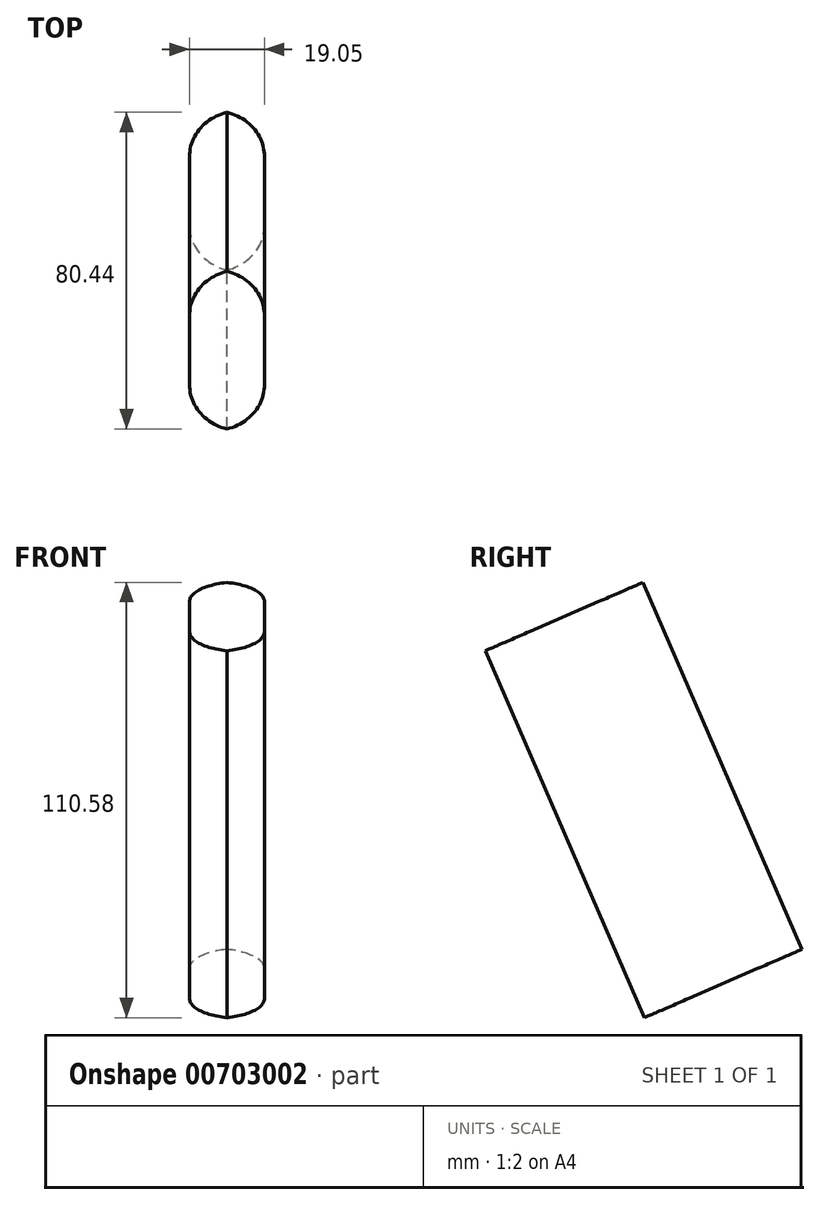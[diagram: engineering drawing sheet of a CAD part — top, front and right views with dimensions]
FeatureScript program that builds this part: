
annotation { "Feature Type Name" : "Feature", "Feature Type Description" : "" }
export const myFeature = defineFeature(function(context is Context, id is Id, definition is map)
    precondition{}
    {
        {
            var Q0;
            Q0=qCreatedBy(makeId("Right.planeOp"),FACE);
            var sketch = newSketch(context, id + "F0", { "sketchPlane" : qUnion([Q0])});
            skLineSegment(sketch, "E0", {"start": v(3.78, 1.74) * mm, "end": v(44.56, 19.41) * mm});
            skLineSegment(sketch, "E1", {"start": v(4.17, 112.64) * mm, "end": v(-36.62, 94.96) * mm});
            skLineSegment(sketch, "E2", {"start": v(44.56, 19.41) * mm, "end": v(4.17, 112.64) * mm});
            skLineSegment(sketch, "E3", {"start": v(3.78, 1.74) * mm, "end": v(-36.62, 94.96) * mm});
            skSolve(sketch);
        }
        {
            var Q0;
            Q0=makeQuery(id+"F0.imprint","IMPRINT",FACE,{"disambiguationData":[TD([[makeQuery(id+"F0.imprint","IMPRINT",EDGE,{"derivedFrom":sQuery(id+"F0.wireOp",EDGE,"E0")}),1.0]])]});
            extrude(context, id + "F1", {"entities" : qUnion([Q0]), "depth" : 19.05 * mm, "offsetDistance" : 25.4 * mm});
        }
        {
            var Q0;
            Q0=makeQuery(id+"F1.opExtrude","CAP_EDGE",EDGE,{"disambiguationData":[OSD([sQuery(id+"F0.wireOp",EDGE,"pg5uUo5L-hMJ6-0TQC-OhPI-5jsaEnWjynJh")])],"isStart":false});
            var Q1;
            Q1=makeQuery(id+"F1.opExtrude","CAP_EDGE",EDGE,{"disambiguationData":[OSD([sQuery(id+"F0.wireOp",EDGE,"pg5uUo5L-hMJ6-0TQC-OhPI-5jsaEnWjynJh")])],"isStart":true});
            var Q2;
            Q2=makeQuery(id+"F1.opExtrude","CAP_EDGE",EDGE,{"disambiguationData":[OSD([sQuery(id+"F0.wireOp",EDGE,"cwDIRSyl-O5Kx-4CkM-n87C-obHUcLD1ZQiq")])],"isStart":false});
            var Q3;
            Q3=makeQuery(id+"F1.opExtrude","CAP_EDGE",EDGE,{"disambiguationData":[OSD([sQuery(id+"F0.wireOp",EDGE,"cwDIRSyl-O5Kx-4CkM-n87C-obHUcLD1ZQiq")])],"isStart":true});
            var Q4;
            Q4=makeQuery(id+"F1.opExtrude","CAP_EDGE",EDGE,{"disambiguationData":[OSD([sQuery(id+"F0.wireOp",EDGE,"E2")])],"isStart":true});
            var Q5;
            Q5=makeQuery(id+"F1.opExtrude","CAP_EDGE",EDGE,{"disambiguationData":[OSD([sQuery(id+"F0.wireOp",EDGE,"E2")])],"isStart":false});
            var Q6;
            Q6=makeQuery(id+"F1.opExtrude","CAP_EDGE",EDGE,{"disambiguationData":[OSD([sQuery(id+"F0.wireOp",EDGE,"E3")])],"isStart":true});
            var Q7;
            Q7=makeQuery(id+"F1.opExtrude","CAP_EDGE",EDGE,{"disambiguationData":[OSD([sQuery(id+"F0.wireOp",EDGE,"E3")])],"isStart":false});
            fillet(context, id + "F2", {"entities" : qUnion([Q0, Q1, Q2, Q3, Q4, Q5, Q6, Q7]), "radius" : 12.7 * mm, "tangentPropagation" : true, "allowEdgeOverflow" : false});
        }
    });
